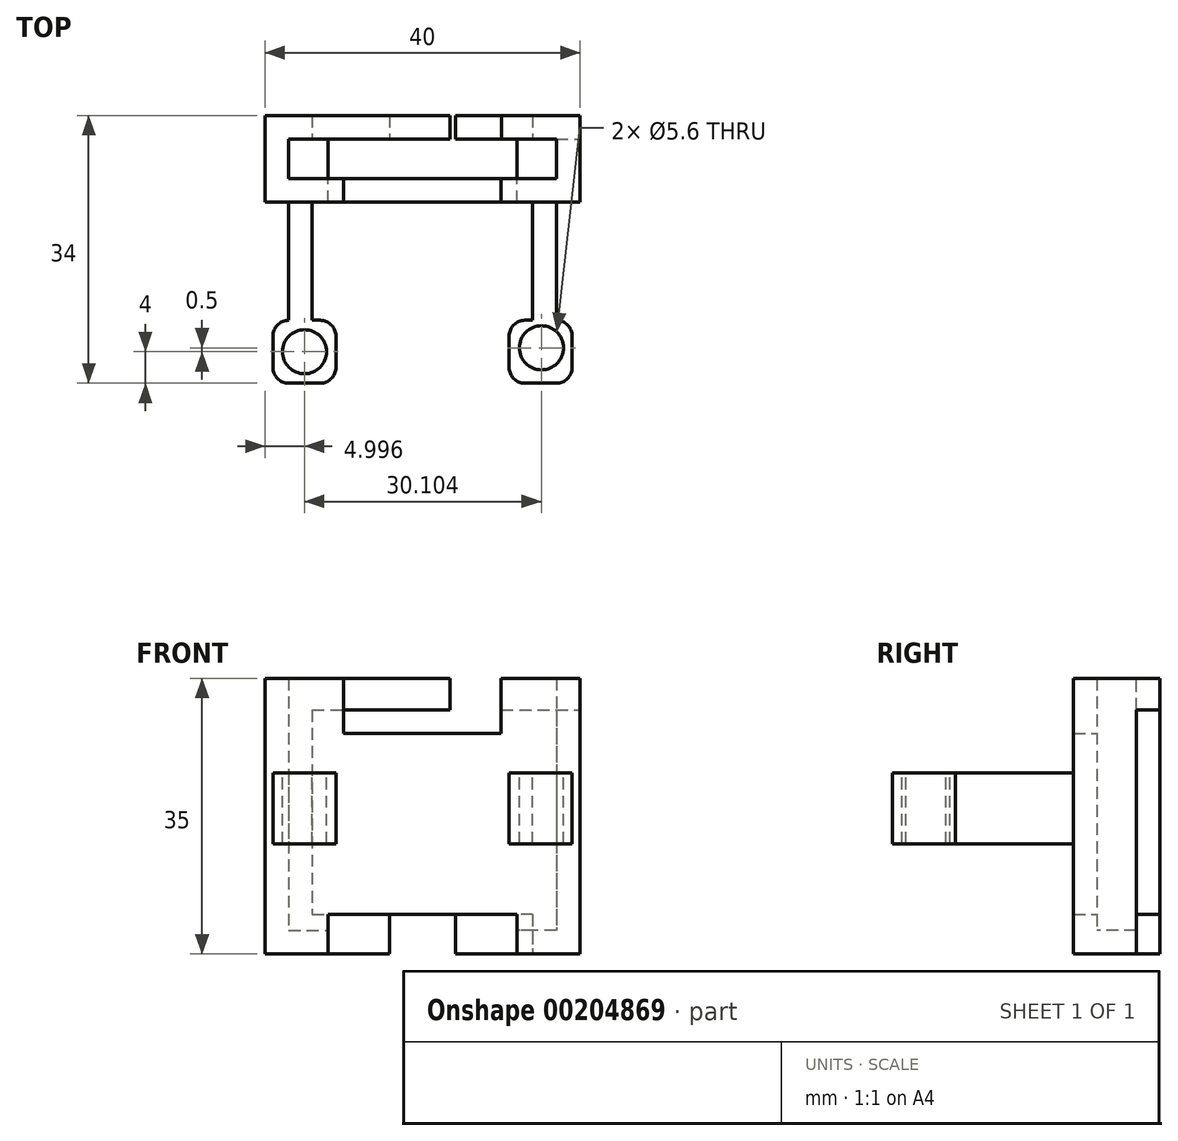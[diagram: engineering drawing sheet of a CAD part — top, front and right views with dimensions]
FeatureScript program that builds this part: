
annotation { "Feature Type Name" : "Feature", "Feature Type Description" : "" }
export const myFeature = defineFeature(function(context is Context, id is Id, definition is map)
    precondition{}
    {
        {
            var Q0;
            Q0=qCreatedBy(makeId("Front.planeOp"),FACE);
            var sketch = newSketch(context, id + "F0", { "sketchPlane" : qUnion([Q0])});
            skLineSegment(sketch, "E0.top", {"start": v(-46.71, 6.56) * mm, "end": v(-41.71, 6.56) * mm});
            skLineSegment(sketch, "E0.left", {"start": v(-46.71, 38.56) * mm, "end": v(-46.71, 6.56) * mm});
            skLineSegment(sketch, "E1", {"start": v(-39.71, 38.56) * mm, "end": v(-39.71, 31.56) * mm});
            skLineSegment(sketch, "E2", {"start": v(-39.71, 31.56) * mm, "end": v(-29.71, 31.56) * mm});
            skLineSegment(sketch, "E3", {"start": v(-46.71, 38.56) * mm, "end": v(-39.71, 38.56) * mm});
            skLineSegment(sketch, "E4", {"start": v(-41.71, 8.56) * mm, "end": v(-41.71, 6.56) * mm});
            skLineSegment(sketch, "E5", {"start": v(-29.71, 31.56) * mm, "end": v(-29.71, 8.56) * mm});
            skLineSegment(sketch, "E6.MirrorCS", {"start": v(-19.71, 38.56) * mm, "end": v(-19.71, 31.56) * mm});
            skLineSegment(sketch, "E7.MirrorCS", {"start": v(-12.71, 6.56) * mm, "end": v(-17.71, 6.56) * mm});
            skLineSegment(sketch, "E8.MirrorCS", {"start": v(-12.71, 38.56) * mm, "end": v(-12.71, 6.56) * mm});
            skLineSegment(sketch, "E9.MirrorCS", {"start": v(-17.71, 8.56) * mm, "end": v(-17.71, 6.56) * mm});
            skLineSegment(sketch, "E10.MirrorCS", {"start": v(-12.71, 38.56) * mm, "end": v(-19.71, 38.56) * mm});
            skLineSegment(sketch, "E11", {"start": v(-41.71, 8.56) * mm, "end": v(-17.71, 8.56) * mm});
            skLineSegment(sketch, "E12", {"start": v(-19.71, 31.56) * mm, "end": v(-29.71, 31.56) * mm});
            skLineSegment(sketch, "E13", {"start": v(-46.71, 21.88) * mm, "end": v(-12.71, 21.88) * mm});
            skSolve(sketch);
        }
        {
            var Q0;
            Q0 = qSketchRegion(id + "F0", true);
            extrude(context, id + "F1", {"entities" : qUnion([Q0]), "endBound" : BoundingType.SYMMETRIC, "depth" : 3 * mm});
        }
        {
            var Q0;
            Q0=makeQuery(id+"F1.opExtrude","CAP_FACE",FACE,{"disambiguationData":[OSD([sQuery(id+"F0.wireOp",EDGE,"E0.top"),sQuery(id+"F0.wireOp",EDGE,"E0.left"),sQuery(id+"F0.wireOp",EDGE,"E1"),sQuery(id+"F0.wireOp",EDGE,"E2"),sQuery(id+"F0.wireOp",EDGE,"hQumlcYS-BVpM-Qe34-Faz5-ovKVB0zx6kEf"),sQuery(id+"F0.wireOp",EDGE,"S4NNzPwl-8fdv-axjF-yAQh-UWlD5xwCHcjv"),sQuery(id+"F0.wireOp",EDGE,"AAgkFRn4-YeC1-ZEBq-ucuP-HGQnwFGHkqqj"),sQuery(id+"F0.wireOp",EDGE,"vNrXK4ta-PUhw-VIRR-P8v9-7VR6Ly27LxA9"),sQuery(id+"F0.wireOp",EDGE,"oesqfkWM-Qq6h-EH4e-nNYl-gxqhzfA0Elxi.bottom"),sQuery(id+"F0.wireOp",EDGE,"oesqfkWM-Qq6h-EH4e-nNYl-gxqhzfA0Elxi.top"),sQuery(id+"F0.wireOp",EDGE,"oesqfkWM-Qq6h-EH4e-nNYl-gxqhzfA0Elxi.left"),sQuery(id+"F0.wireOp",EDGE,"oesqfkWM-Qq6h-EH4e-nNYl-gxqhzfA0Elxi.right"),sQuery(id+"F0.wireOp",EDGE,"E3"),sQuery(id+"F0.wireOp",EDGE,"E4"),sQuery(id+"F0.wireOp",EDGE,"9299d5dc-cd4b-4c38-ba6e-99de386c7c660.MirrorCS"),sQuery(id+"F0.wireOp",EDGE,"9299d5dc-cd4b-4c38-ba6e-99de386c7c662.MirrorCS"),sQuery(id+"F0.wireOp",EDGE,"9299d5dc-cd4b-4c38-ba6e-99de386c7c663.MirrorCS"),sQuery(id+"F0.wireOp",EDGE,"9299d5dc-cd4b-4c38-ba6e-99de386c7c664.MirrorCS"),sQuery(id+"F0.wireOp",EDGE,"E7.MirrorCS"),sQuery(id+"F0.wireOp",EDGE,"E8.MirrorCS"),sQuery(id+"F0.wireOp",EDGE,"E6.MirrorCS"),sQuery(id+"F0.wireOp",EDGE,"9299d5dc-cd4b-4c38-ba6e-99de386c7c669.MirrorCS"),sQuery(id+"F0.wireOp",EDGE,"E9.MirrorCS"),sQuery(id+"F0.wireOp",EDGE,"E61.MirrorCS"),sQuery(id+"F0.wireOp",EDGE,"E62.MirrorCS"),sQuery(id+"F0.wireOp",EDGE,"E10.MirrorCS"),sQuery(id+"F0.wireOp",EDGE,"E64.MirrorCS"),sQuery(id+"F0.wireOp",EDGE,"E11"),sQuery(id+"F0.wireOp",EDGE,"E12")])],"isStart":false});
            var sketch = newSketch(context, id + "F2", { "sketchPlane" : qUnion([Q0])});
            skLineSegment(sketch, "E14", {"start": v(-46.71, 6.56) * mm, "end": v(-46.71, 17.56) * mm});
            skLineSegment(sketch, "E15.bottom", {"start": v(-46.71, 17.56) * mm, "end": v(-43.71, 17.56) * mm});
            skLineSegment(sketch, "E15.top", {"start": v(-46.71, 26.56) * mm, "end": v(-43.71, 26.56) * mm});
            skLineSegment(sketch, "E15.left", {"start": v(-46.71, 17.56) * mm, "end": v(-46.71, 26.56) * mm});
            skLineSegment(sketch, "E15.right", {"start": v(-43.71, 17.56) * mm, "end": v(-43.71, 26.56) * mm});
            skLineSegment(sketch, "E16", {"start": v(-29.71, 31.56) * mm, "end": v(-29.71, 8.56) * mm});
            skLineSegment(sketch, "E17.MirrorCS", {"start": v(-12.71, 17.56) * mm, "end": v(-15.71, 17.56) * mm});
            skLineSegment(sketch, "E18.MirrorCS", {"start": v(-12.71, 17.56) * mm, "end": v(-12.71, 26.56) * mm});
            skLineSegment(sketch, "E19.MirrorCS", {"start": v(-15.71, 17.56) * mm, "end": v(-15.71, 26.56) * mm});
            skLineSegment(sketch, "E20.MirrorCS", {"start": v(-12.71, 6.56) * mm, "end": v(-12.71, 17.56) * mm});
            skLineSegment(sketch, "E21.MirrorCS", {"start": v(-12.71, 26.56) * mm, "end": v(-15.71, 26.56) * mm});
            skSolve(sketch);
        }
        {
            var Q0;
            Q0=makeQuery(id+"F2.imprint","IMPRINT",FACE,{"disambiguationData":[TD([[makeQuery(id+"F2.imprint","IMPRINT",EDGE,{"derivedFrom":sQuery(id+"F2.wireOp",EDGE,"E15.bottom")}),1.0]])]});
            var Q1;
            Q1=makeQuery(id+"F2.imprint","IMPRINT",FACE,{"disambiguationData":[TD([[makeQuery(id+"F2.imprint","IMPRINT",EDGE,{"derivedFrom":sQuery(id+"F2.wireOp",EDGE,"E17.MirrorCS")}),-1.0]])]});
            extrude(context, id + "F3", {"entities" : qUnion([Q0, Q1]), "operationType" : NewBodyOperationType.ADD, "depth" : 15 * mm});
        }
        {
            var Q0;
            Q0=makeQuery(id+"F3.opExtrude","CAP_FACE",FACE,{"disambiguationData":[OSD([sQuery(id+"F2.wireOp",EDGE,"E15.bottom"),sQuery(id+"F2.wireOp",EDGE,"E15.top"),sQuery(id+"F2.wireOp",EDGE,"E15.left"),sQuery(id+"F2.wireOp",EDGE,"E15.right")])],"isStart":false});
            var sketch = newSketch(context, id + "F4", { "sketchPlane" : qUnion([Q0])});
            skLineSegment(sketch, "E22.bottom", {"start": v(-46.71, 26.56) * mm, "end": v(-43.71, 26.56) * mm});
            skLineSegment(sketch, "E22.top", {"start": v(-46.71, 17.56) * mm, "end": v(-43.71, 17.56) * mm});
            skLineSegment(sketch, "E22.left", {"start": v(-46.71, 26.56) * mm, "end": v(-46.71, 17.56) * mm});
            skLineSegment(sketch, "E23.MirrorCS", {"start": v(-12.71, 26.56) * mm, "end": v(-15.71, 26.56) * mm});
            skLineSegment(sketch, "E24.MirrorCS", {"start": v(-12.71, 26.56) * mm, "end": v(-12.71, 17.56) * mm});
            skLineSegment(sketch, "E25.MirrorCS", {"start": v(-12.71, 17.56) * mm, "end": v(-15.71, 17.56) * mm});
            skLineSegment(sketch, "E26", {"start": v(-15.71, 22.06) * mm, "end": v(-14.71, 22.06) * mm});
            skLineSegment(sketch, "E27", {"start": v(-44.71, 26.56) * mm, "end": v(-48.71, 26.56) * mm});
            skLineSegment(sketch, "E28", {"start": v(-44.71, 26.56) * mm, "end": v(-40.71, 26.56) * mm});
            skLineSegment(sketch, "E29.bottom", {"start": v(-48.71, 26.56) * mm, "end": v(-40.71, 26.56) * mm});
            skLineSegment(sketch, "E29.top", {"start": v(-48.71, 17.56) * mm, "end": v(-40.71, 17.56) * mm});
            skLineSegment(sketch, "E29.left", {"start": v(-48.71, 26.56) * mm, "end": v(-48.71, 17.56) * mm});
            skLineSegment(sketch, "E29.right", {"start": v(-40.71, 26.56) * mm, "end": v(-40.71, 17.56) * mm});
            skPoint(sketch, "E30.start.orphan", {"position": v(-43.71, 22.06) * mm});
            skPoint(sketch, "E31", {"position": v(-44.71, 22.06) * mm});
            skPoint(sketch, "E32.end.orphan", {"position": v(-44.71, 17.56) * mm});
            skLineSegment(sketch, "E33.MirrorCS", {"start": v(-14.71, 26.56) * mm, "end": v(-10.71, 26.56) * mm});
            skLineSegment(sketch, "E34.MirrorCS", {"start": v(-14.71, 26.56) * mm, "end": v(-18.71, 26.56) * mm});
            skPoint(sketch, "E35.MirrorP", {"position": v(-14.71, 17.56) * mm});
            skLineSegment(sketch, "E36.MirrorCS", {"start": v(-18.71, 26.56) * mm, "end": v(-18.71, 17.56) * mm});
            skLineSegment(sketch, "E37.MirrorCS", {"start": v(-10.71, 17.56) * mm, "end": v(-18.71, 17.56) * mm});
            skLineSegment(sketch, "E38.MirrorCS", {"start": v(-10.71, 26.56) * mm, "end": v(-10.71, 17.56) * mm});
            skPoint(sketch, "E39.MirrorP", {"position": v(-15.71, 22.06) * mm});
            skPoint(sketch, "E40.MirrorP", {"position": v(-14.71, 22.06) * mm});
            skLineSegment(sketch, "E41.MirrorCS", {"start": v(-10.71, 26.56) * mm, "end": v(-18.71, 26.56) * mm});
            skSolve(sketch);
        }
        {
            var Q0;
            Q0 = qSketchRegion(id + "F4", true);
            extrude(context, id + "F5", {"entities" : qUnion([Q0]), "operationType" : NewBodyOperationType.ADD, "depth" : 8 * mm});
        }
        {
            var Q0;
            Q0=makeQuery(id+"F5.boolean.opBoolean","MERGE",FACE,{"derivedFrom":[makeQuery(id+"F3.opExtrude","SWEPT_FACE",FACE,{"disambiguationData":[OSD([sQuery(id+"F2.wireOp",EDGE,"E15.top")])]}),makeQuery(id+"F5.opExtrude","SWEPT_FACE",FACE,{"disambiguationData":[OSD([sQuery(id+"F4.wireOp",EDGE,"E29.bottom")])]})]});
            var sketch = newSketch(context, id + "F6", { "sketchPlane" : qUnion([Q0])});
            skLineSegment(sketch, "E42", {"start": v(-40.71, -24.5) * mm, "end": v(-40.71, -16.5) * mm});
            skPoint(sketch, "E43", {"position": v(-44.71, -20.5) * mm});
            skPoint(sketch, "E44.orphan", {"position": v(-48.71, -16.5) * mm});
            skPoint(sketch, "E45.MirrorP", {"position": v(-14.61, -20) * mm});
            skPoint(sketch, "E46.start.orphan", {"position": v(-29.66, 0) * mm});
            skSolve(sketch);
        }
        {
            var Q0;
            Q0=sQuery(id+"F6.wireOp",VERTEX,"E43");
            var Q1;
            Q1=sQuery(id+"F6.wireOp",VERTEX,"E45.MirrorP");
            var Q2;
            Q2=makeQuery(id+"F1.opExtrude","SWEPT_BODY",BODY,{"disambiguationData":[OSD([sQuery(id+"F0.wireOp",EDGE,"E0.top"),sQuery(id+"F0.wireOp",EDGE,"E0.left"),sQuery(id+"F0.wireOp",EDGE,"E1"),sQuery(id+"F0.wireOp",EDGE,"E2"),sQuery(id+"F0.wireOp",EDGE,"hQumlcYS-BVpM-Qe34-Faz5-ovKVB0zx6kEf"),sQuery(id+"F0.wireOp",EDGE,"S4NNzPwl-8fdv-axjF-yAQh-UWlD5xwCHcjv"),sQuery(id+"F0.wireOp",EDGE,"AAgkFRn4-YeC1-ZEBq-ucuP-HGQnwFGHkqqj"),sQuery(id+"F0.wireOp",EDGE,"vNrXK4ta-PUhw-VIRR-P8v9-7VR6Ly27LxA9"),sQuery(id+"F0.wireOp",EDGE,"oesqfkWM-Qq6h-EH4e-nNYl-gxqhzfA0Elxi.bottom"),sQuery(id+"F0.wireOp",EDGE,"oesqfkWM-Qq6h-EH4e-nNYl-gxqhzfA0Elxi.top"),sQuery(id+"F0.wireOp",EDGE,"oesqfkWM-Qq6h-EH4e-nNYl-gxqhzfA0Elxi.left"),sQuery(id+"F0.wireOp",EDGE,"oesqfkWM-Qq6h-EH4e-nNYl-gxqhzfA0Elxi.right"),sQuery(id+"F0.wireOp",EDGE,"E3"),sQuery(id+"F0.wireOp",EDGE,"E4"),sQuery(id+"F0.wireOp",EDGE,"9299d5dc-cd4b-4c38-ba6e-99de386c7c660.MirrorCS"),sQuery(id+"F0.wireOp",EDGE,"9299d5dc-cd4b-4c38-ba6e-99de386c7c662.MirrorCS"),sQuery(id+"F0.wireOp",EDGE,"9299d5dc-cd4b-4c38-ba6e-99de386c7c663.MirrorCS"),sQuery(id+"F0.wireOp",EDGE,"9299d5dc-cd4b-4c38-ba6e-99de386c7c664.MirrorCS"),sQuery(id+"F0.wireOp",EDGE,"E7.MirrorCS"),sQuery(id+"F0.wireOp",EDGE,"E8.MirrorCS"),sQuery(id+"F0.wireOp",EDGE,"E6.MirrorCS"),sQuery(id+"F0.wireOp",EDGE,"9299d5dc-cd4b-4c38-ba6e-99de386c7c669.MirrorCS"),sQuery(id+"F0.wireOp",EDGE,"E9.MirrorCS"),sQuery(id+"F0.wireOp",EDGE,"E61.MirrorCS"),sQuery(id+"F0.wireOp",EDGE,"E62.MirrorCS"),sQuery(id+"F0.wireOp",EDGE,"E10.MirrorCS"),sQuery(id+"F0.wireOp",EDGE,"E64.MirrorCS"),sQuery(id+"F0.wireOp",EDGE,"E11"),sQuery(id+"F0.wireOp",EDGE,"E12")])]});
            hole(context, id + "F7", {"style" : HoleStyle.SIMPLE, "endStyle" : HoleEndStyle.THROUGH, "holeDiameter" : 5.6 * mm, "locations" : qUnion([Q0, Q1]), "scope" : qUnion([Q2]), "isTappedThrough" : true});
        }
        {
            var Q0;
            Q0=makeQuery(id+"F5.opExtrude","CAP_EDGE",EDGE,{"disambiguationData":[OSD([sQuery(id+"F4.wireOp",EDGE,"E38.MirrorCS")])],"isStart":true});
            var Q1;
            Q1=makeQuery(id+"F5.opExtrude","CAP_EDGE",EDGE,{"disambiguationData":[OSD([sQuery(id+"F4.wireOp",EDGE,"E36.MirrorCS")])],"isStart":true});
            var Q2;
            Q2=makeQuery(id+"F5.opExtrude","CAP_EDGE",EDGE,{"disambiguationData":[OSD([sQuery(id+"F4.wireOp",EDGE,"E36.MirrorCS")])],"isStart":false});
            var Q3;
            Q3=makeQuery(id+"F5.opExtrude","CAP_EDGE",EDGE,{"disambiguationData":[OSD([sQuery(id+"F4.wireOp",EDGE,"E38.MirrorCS")])],"isStart":false});
            var Q4;
            Q4=makeQuery(id+"F5.opExtrude","CAP_EDGE",EDGE,{"disambiguationData":[OSD([sQuery(id+"F4.wireOp",EDGE,"E29.left")])],"isStart":false});
            var Q5;
            Q5=makeQuery(id+"F5.opExtrude","CAP_EDGE",EDGE,{"disambiguationData":[OSD([sQuery(id+"F4.wireOp",EDGE,"E29.left")])],"isStart":true});
            var Q6;
            Q6=makeQuery(id+"F5.opExtrude","CAP_EDGE",EDGE,{"disambiguationData":[OSD([sQuery(id+"F4.wireOp",EDGE,"E29.right")])],"isStart":true});
            var Q7;
            Q7=makeQuery(id+"F5.opExtrude","CAP_EDGE",EDGE,{"disambiguationData":[OSD([sQuery(id+"F4.wireOp",EDGE,"E29.right")])],"isStart":false});
            fillet(context, id + "F8", {"entities" : qUnion([Q0, Q1, Q2, Q3, Q4, Q5, Q6, Q7]), "radius" : 2 * mm, "tangentPropagation" : true, "allowEdgeOverflow" : false});
        }
        {
            var Q0;
            Q0=makeQuery(id+"F1.opExtrude","CAP_FACE",FACE,{"disambiguationData":[OSD([sQuery(id+"F0.wireOp",EDGE,"E0.top"),sQuery(id+"F0.wireOp",EDGE,"E0.left"),sQuery(id+"F0.wireOp",EDGE,"E1"),sQuery(id+"F0.wireOp",EDGE,"E2"),sQuery(id+"F0.wireOp",EDGE,"E3"),sQuery(id+"F0.wireOp",EDGE,"E4"),sQuery(id+"F0.wireOp",EDGE,"E7.MirrorCS"),sQuery(id+"F0.wireOp",EDGE,"E8.MirrorCS"),sQuery(id+"F0.wireOp",EDGE,"E6.MirrorCS"),sQuery(id+"F0.wireOp",EDGE,"E9.MirrorCS"),sQuery(id+"F0.wireOp",EDGE,"E10.MirrorCS"),sQuery(id+"F0.wireOp",EDGE,"E11"),sQuery(id+"F0.wireOp",EDGE,"E12")])],"isStart":true});
            var sketch = newSketch(context, id + "F9", { "sketchPlane" : qUnion([Q0])});
            skLineSegment(sketch, "E47.bottom", {"start": v(12.71, 38.56) * mm, "end": v(9.71, 38.56) * mm});
            skLineSegment(sketch, "E47.top", {"start": v(12.71, 3.56) * mm, "end": v(9.71, 3.56) * mm});
            skLineSegment(sketch, "E47.left", {"start": v(12.71, 38.56) * mm, "end": v(12.71, 3.56) * mm});
            skLineSegment(sketch, "E47.right", {"start": v(9.71, 38.56) * mm, "end": v(9.71, 3.56) * mm});
            skLineSegment(sketch, "E48", {"start": v(17.71, 6.56) * mm, "end": v(17.71, 3.56) * mm});
            skLineSegment(sketch, "E49", {"start": v(17.71, 3.56) * mm, "end": v(12.71, 3.56) * mm});
            skLineSegment(sketch, "E50.MirrorCS", {"start": v(41.71, 3.56) * mm, "end": v(46.71, 3.56) * mm});
            skLineSegment(sketch, "E51.MirrorCS", {"start": v(41.71, 6.56) * mm, "end": v(41.71, 3.56) * mm});
            skLineSegment(sketch, "E52.MirrorCS", {"start": v(49.71, 38.56) * mm, "end": v(49.71, 3.56) * mm});
            skLineSegment(sketch, "E53.MirrorCS", {"start": v(46.71, 38.56) * mm, "end": v(46.71, 3.56) * mm});
            skLineSegment(sketch, "E54.MirrorCS", {"start": v(46.71, 3.56) * mm, "end": v(49.71, 3.56) * mm});
            skLineSegment(sketch, "E55.MirrorCS", {"start": v(46.71, 38.56) * mm, "end": v(49.71, 38.56) * mm});
            skSolve(sketch);
        }
        {
            var Q0;
            {var subQ3=sQuery(id+"F9.wireOp",EDGE,"E47.bottom");Q0=makeQuery(id+"F9.imprint","IMPRINT",FACE,{"disambiguationData":[TD([[makeQuery(id+"F9.imprint","IMPRINT",EDGE,{"derivedFrom":subQ3}),1.0]])]});}
            var Q1;
            Q1=makeQuery(id+"F9.imprint","IMPRINT",FACE,{"disambiguationData":[TD([[makeQuery(id+"F9.imprint","IMPRINT",EDGE,{"derivedFrom":sQuery(id+"F9.wireOp",EDGE,"E48")}),-1.0]])]});
            var Q2;
            {var subQ0=sQuery(id+"F9.wireOp",EDGE,"E50.MirrorCS");Q2=makeQuery(id+"F9.imprint","IMPRINT",FACE,{"disambiguationData":[TD([[makeQuery(id+"F9.imprint","IMPRINT",EDGE,{"derivedFrom":subQ0}),1.0]])]});}
            var Q3;
            Q3=makeQuery(id+"F9.imprint","IMPRINT",FACE,{"disambiguationData":[TD([[makeQuery(id+"F9.imprint","IMPRINT",EDGE,{"derivedFrom":sQuery(id+"F9.wireOp",EDGE,"E52.MirrorCS")}),-1.0]])]});
            extrude(context, id + "F10", {"entities" : qUnion([Q0, Q1, Q2, Q3]), "operationType" : NewBodyOperationType.ADD, "endBound" : BoundingType.SYMMETRIC, "depth" : 6 * mm});
        }
        {
            var Q0;
            Q0=makeQuery(id+"F10.opExtrude","CAP_FACE",FACE,{"disambiguationData":[OSD([sQuery(id+"F0.wireOp",EDGE,"E0.top"),sQuery(id+"F9.wireOp",EDGE,"E50.MirrorCS"),sQuery(id+"F9.wireOp",EDGE,"E51.MirrorCS"),sQuery(id+"F9.wireOp",EDGE,"E52.MirrorCS"),sQuery(id+"F9.wireOp",EDGE,"E53.MirrorCS"),sQuery(id+"F9.wireOp",EDGE,"E54.MirrorCS"),sQuery(id+"F9.wireOp",EDGE,"E55.MirrorCS")])],"isStart":false});
            var sketch = newSketch(context, id + "F11", { "sketchPlane" : qUnion([Q0])});
            skLineSegment(sketch, "E56", {"start": v(49.71, 38.56) * mm, "end": v(49.71, 3.56) * mm});
            skLineSegment(sketch, "E57", {"start": v(49.71, 3.56) * mm, "end": v(41.71, 3.56) * mm});
            skLineSegment(sketch, "E58", {"start": v(41.71, 3.56) * mm, "end": v(41.71, 6.56) * mm});
            skLineSegment(sketch, "E59", {"start": v(41.71, 6.56) * mm, "end": v(46.71, 6.56) * mm});
            skLineSegment(sketch, "E60", {"start": v(46.71, 6.56) * mm, "end": v(46.71, 38.56) * mm});
            skLineSegment(sketch, "E61", {"start": v(46.71, 38.56) * mm, "end": v(49.71, 38.56) * mm});
            skLineSegment(sketch, "E62.MirrorCS", {"start": v(12.71, 38.56) * mm, "end": v(9.71, 38.56) * mm});
            skLineSegment(sketch, "E63.MirrorCS", {"start": v(12.71, 6.56) * mm, "end": v(12.71, 38.56) * mm});
            skLineSegment(sketch, "E64.MirrorCS", {"start": v(17.71, 6.56) * mm, "end": v(12.71, 6.56) * mm});
            skLineSegment(sketch, "E65.MirrorCS", {"start": v(17.71, 3.56) * mm, "end": v(17.71, 6.56) * mm});
            skLineSegment(sketch, "E66.MirrorCS", {"start": v(9.71, 38.56) * mm, "end": v(9.71, 3.56) * mm});
            skLineSegment(sketch, "E67.MirrorCS", {"start": v(9.71, 3.56) * mm, "end": v(17.71, 3.56) * mm});
            skSolve(sketch);
        }
        {
            var Q0;
            Q0=makeQuery(id+"F11.imprint","IMPRINT",FACE,{"disambiguationData":[TD([[makeQuery(id+"F11.imprint","IMPRINT",EDGE,{"derivedFrom":sQuery(id+"F11.wireOp",EDGE,"E56")}),-1.0]])]});
            extrude(context, id + "F12", {"entities" : qUnion([Q0]), "operationType" : NewBodyOperationType.ADD, "depth" : 2 * mm});
        }
        {
            var Q0;
            Q0=makeQuery(id+"F10.opExtrude","CAP_FACE",FACE,{"disambiguationData":[OSD([sQuery(id+"F0.wireOp",EDGE,"E7.MirrorCS"),sQuery(id+"F9.wireOp",EDGE,"E47.bottom"),sQuery(id+"F9.wireOp",EDGE,"E47.top"),sQuery(id+"F9.wireOp",EDGE,"E47.left"),sQuery(id+"F9.wireOp",EDGE,"E47.right"),sQuery(id+"F9.wireOp",EDGE,"E48"),sQuery(id+"F9.wireOp",EDGE,"E49")])],"isStart":false});
            extrude(context, id + "F13", {"entities" : qUnion([Q0]), "operationType" : NewBodyOperationType.ADD, "depth" : 2 * mm});
        }
        {
            var Q0;
            Q0=makeQuery(id+"F12.opExtrude","CAP_FACE",FACE,{"disambiguationData":[OSD([sQuery(id+"F11.wireOp",EDGE,"E56"),sQuery(id+"F11.wireOp",EDGE,"E57"),sQuery(id+"F11.wireOp",EDGE,"E58"),sQuery(id+"F11.wireOp",EDGE,"E59"),sQuery(id+"F11.wireOp",EDGE,"E60"),sQuery(id+"F11.wireOp",EDGE,"E61")])],"isStart":false});
            var sketch = newSketch(context, id + "F14", { "sketchPlane" : qUnion([Q0])});
            skLineSegment(sketch, "E68.bottom", {"start": v(49.71, 38.56) * mm, "end": v(9.71, 38.56) * mm});
            skLineSegment(sketch, "E68.top", {"start": v(49.71, 34.56) * mm, "end": v(9.71, 34.56) * mm});
            skLineSegment(sketch, "E68.left", {"start": v(49.71, 38.56) * mm, "end": v(49.71, 34.56) * mm});
            skLineSegment(sketch, "E68.right", {"start": v(9.71, 38.56) * mm, "end": v(9.71, 34.56) * mm});
            skLineSegment(sketch, "E69.bottom", {"start": v(9.71, 34.56) * mm, "end": v(15.71, 34.56) * mm});
            skLineSegment(sketch, "E69.top", {"start": v(9.71, 3.56) * mm, "end": v(15.71, 3.56) * mm});
            skLineSegment(sketch, "E69.left", {"start": v(9.71, 34.56) * mm, "end": v(9.71, 3.56) * mm});
            skLineSegment(sketch, "E69.right", {"start": v(15.71, 34.56) * mm, "end": v(15.71, 3.56) * mm});
            skLineSegment(sketch, "E70.bottom", {"start": v(15.71, 3.56) * mm, "end": v(25.54, 3.56) * mm});
            skLineSegment(sketch, "E70.top", {"start": v(15.71, 8.56) * mm, "end": v(25.54, 8.56) * mm});
            skLineSegment(sketch, "E70.left", {"start": v(15.71, 3.56) * mm, "end": v(15.71, 8.56) * mm});
            skLineSegment(sketch, "E70.right", {"start": v(25.54, 3.56) * mm, "end": v(25.54, 8.56) * mm});
            skLineSegment(sketch, "E71.MirrorCS", {"start": v(49.71, 3.56) * mm, "end": v(43.71, 3.56) * mm});
            skLineSegment(sketch, "E72.MirrorCS", {"start": v(43.71, 3.56) * mm, "end": v(33.89, 3.56) * mm});
            skLineSegment(sketch, "E73.MirrorCS", {"start": v(43.71, 8.56) * mm, "end": v(33.89, 8.56) * mm});
            skLineSegment(sketch, "E74.MirrorCS", {"start": v(43.71, 3.56) * mm, "end": v(43.71, 8.56) * mm});
            skLineSegment(sketch, "E75.MirrorCS", {"start": v(33.89, 3.56) * mm, "end": v(33.89, 8.56) * mm});
            skLineSegment(sketch, "E76.MirrorCS", {"start": v(49.71, 34.56) * mm, "end": v(43.71, 34.56) * mm});
            skLineSegment(sketch, "E77.MirrorCS", {"start": v(49.71, 34.56) * mm, "end": v(49.71, 3.56) * mm});
            skLineSegment(sketch, "E78.MirrorCS", {"start": v(43.71, 34.56) * mm, "end": v(43.71, 3.56) * mm});
            skSolve(sketch);
        }
        {
            var Q0;
            {var subQ1=sQuery(id+"F14.wireOp",EDGE,"E68.top");Q0=makeQuery(id+"F14.imprint","IMPRINT",FACE,{"disambiguationData":[TD([[makeQuery(id+"F14.imprint","IMPRINT",EDGE,{"derivedFrom":subQ1}),-1.0]])]});}
            var Q1;
            {var subQ1=sQuery(id+"F14.wireOp",EDGE,"E71.MirrorCS");Q1=makeQuery(id+"F14.imprint","IMPRINT",FACE,{"disambiguationData":[TD([[makeQuery(id+"F14.imprint","IMPRINT",EDGE,{"derivedFrom":subQ1}),1.0]])]});}
            var Q2;
            {var subQ3=sQuery(id+"F14.wireOp",EDGE,"E75.MirrorCS");Q2=makeQuery(id+"F14.imprint","IMPRINT",FACE,{"disambiguationData":[TD([[makeQuery(id+"F14.imprint","IMPRINT",EDGE,{"derivedFrom":subQ3}),-1.0]])]});}
            var Q3;
            {var subQ5=makeQuery(id+"F12.opExtrude","CAP_EDGE",EDGE,{"disambiguationData":[OSD([sQuery(id+"F11.wireOp",EDGE,"E58")])],"isStart":false});Q3=makeQuery(id+"F14.imprint","IMPRINT",FACE,{"disambiguationData":[TD([[makeQuery(id+"F14.imprint","IMPRINT",EDGE,{"derivedFrom":subQ5}),1.0]])]});}
            var Q4;
            Q4=makeQuery(id+"F14.imprint","IMPRINT",FACE,{"disambiguationData":[TD([[makeQuery(id+"F14.imprint","IMPRINT",EDGE,{"derivedFrom":sQuery(id+"F14.wireOp",EDGE,"E70.bottom")}),1.0]])]});
            var Q5;
            Q5=makeQuery(id+"F14.imprint","IMPRINT",FACE,{"disambiguationData":[TD([[makeQuery(id+"F14.imprint","IMPRINT",EDGE,{"derivedFrom":sQuery(id+"F14.wireOp",EDGE,"E69.bottom")}),-1.0]])]});
            var Q6;
            {var subQ3=sQuery(id+"F14.wireOp",EDGE,"E68.left");Q6=makeQuery(id+"F14.imprint","IMPRINT",FACE,{"disambiguationData":[TD([[makeQuery(id+"F14.imprint","IMPRINT",EDGE,{"derivedFrom":subQ3}),-1.0]])]});}
            var Q7;
            {var subQ3=sQuery(id+"F14.wireOp",EDGE,"E78.MirrorCS");var subQ5=makeQuery(id+"F14.imprint","INTERSECT",VERTEX,{"derivedFrom":[subQ3,sQuery(id+"F14.wireOp",EDGE,"E73.MirrorCS")]});Q7=makeQuery(id+"F14.imprint","IMPRINT",FACE,{"disambiguationData":[TD([[makeQuery(id+"F14.imprint","IMPRINT",EDGE,{"disambiguationData":[TD([[subQ5,-1.0]])],"derivedFrom":subQ3}),1.0]])]});}
            extrude(context, id + "F15", {"entities" : qUnion([Q0, Q1, Q2, Q3, Q4, Q5, Q6, Q7]), "operationType" : NewBodyOperationType.ADD, "depth" : 3 * mm});
        }
        {
            var Q0;
            Q0=makeQuery(id+"F15.opExtrude","CAP_FACE",FACE,{"disambiguationData":[OSD([sQuery(id+"F14.wireOp",EDGE,"E68.bottom"),sQuery(id+"F14.wireOp",EDGE,"E68.top"),sQuery(id+"F14.wireOp",EDGE,"E68.left"),sQuery(id+"F14.wireOp",EDGE,"E68.right"),sQuery(id+"F14.wireOp",EDGE,"E69.top"),sQuery(id+"F14.wireOp",EDGE,"E69.left"),sQuery(id+"F14.wireOp",EDGE,"E69.right"),sQuery(id+"F14.wireOp",EDGE,"E70.bottom"),sQuery(id+"F14.wireOp",EDGE,"E70.top"),sQuery(id+"F14.wireOp",EDGE,"E70.right"),sQuery(id+"F14.wireOp",EDGE,"E75.MirrorCS"),sQuery(id+"F14.wireOp",EDGE,"E71.MirrorCS"),sQuery(id+"F14.wireOp",EDGE,"E77.MirrorCS"),sQuery(id+"F14.wireOp",EDGE,"E78.MirrorCS"),sQuery(id+"F14.wireOp",EDGE,"E72.MirrorCS"),sQuery(id+"F14.wireOp",EDGE,"E73.MirrorCS")])],"isStart":false});
            var sketch = newSketch(context, id + "F16", { "sketchPlane" : qUnion([Q0])});
            skLineSegment(sketch, "E79", {"start": v(19.69, 38.56) * mm, "end": v(19.69, 34.56) * mm});
            skLineSegment(sketch, "E80", {"start": v(19.69, 34.56) * mm, "end": v(26.19, 34.56) * mm});
            skLineSegment(sketch, "E81", {"start": v(26.19, 34.56) * mm, "end": v(26.19, 38.56) * mm});
            skLineSegment(sketch, "E82", {"start": v(26.19, 38.56) * mm, "end": v(19.69, 38.56) * mm});
            skSolve(sketch);
        }
        {
            var Q0;
            Q0=makeQuery(id+"F16.imprint","IMPRINT",FACE,{"disambiguationData":[TD([[makeQuery(id+"F16.imprint","IMPRINT",EDGE,{"derivedFrom":sQuery(id+"F16.wireOp",EDGE,"E79")}),1.0]])]});
            extrude(context, id + "F17", {"entities" : qUnion([Q0]), "operationType" : NewBodyOperationType.REMOVE, "oppositeDirection" : true, "depth" : 3 * mm});
        }
    });
